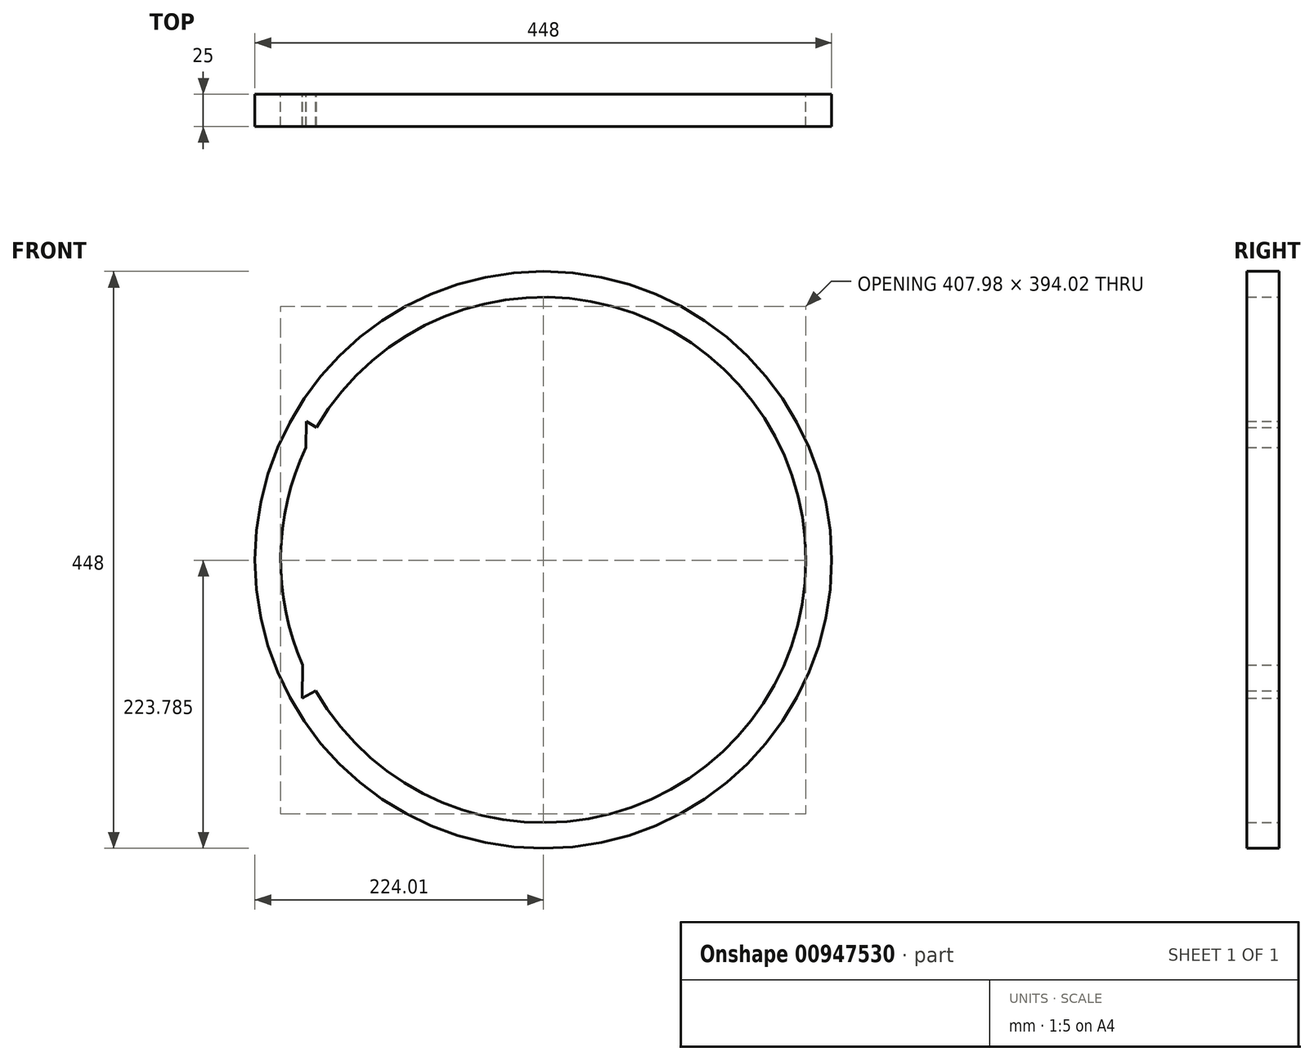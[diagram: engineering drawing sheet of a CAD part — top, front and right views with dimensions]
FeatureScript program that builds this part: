
annotation { "Feature Type Name" : "Feature", "Feature Type Description" : "" }
export const myFeature = defineFeature(function(context is Context, id is Id, definition is map)
    precondition{}
    {
        {
            var Q0;
            Q0=qCreatedBy(makeId("Front.planeOp"),FACE);
            var sketch = newSketch(context, id + "F0", { "sketchPlane" : qUnion([Q0])});
            skCircle(sketch, "E0", {"center": v(0, 0) * mm, "radius": 224 * mm});
            skCircle(sketch, "E1", {"center": v(0, 0) * mm, "radius": 204 * mm});
            skLineSegment(sketch, "E2", {"start": v(0, 0) * mm, "end": v(-204, 0) * mm});
            skLineSegment(sketch, "E3", {"start": v(-176.38, -102.5) * mm, "end": v(-176.38, 102.5) * mm});
            skLineSegment(sketch, "E4", {"start": v(0, 0) * mm, "end": v(-194.28, -111.5) * mm});
            skLineSegment(sketch, "E5", {"start": v(0, 0) * mm, "end": v(-193.37, 113.07) * mm});
            skLineSegment(sketch, "E6", {"start": v(-187.28, -107.47) * mm, "end": v(-184.13, 107.67) * mm});
            skLineSegment(sketch, "E7", {"start": v(-176.38, -49.3) * mm, "end": v(-186.38, -46.1) * mm});
            skSolve(sketch);
        }
        {
            var Q0;
            Q0 = qSketchRegion(id + "F0", true);
            extrude(context, id + "F1", {"entities" : qUnion([Q0]), "depth" : 25 * mm, "offsetDistance" : 25 * mm});
        }
    });
